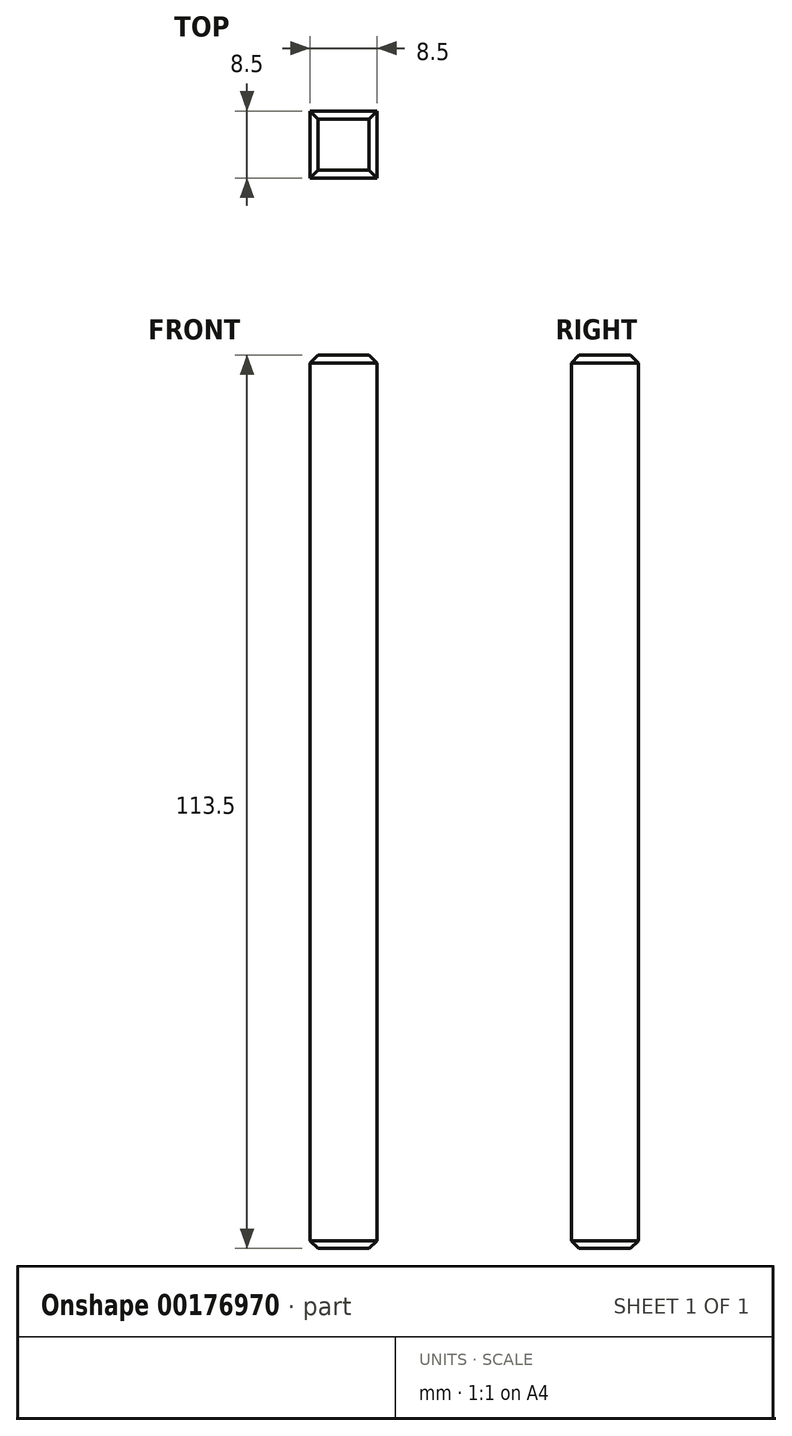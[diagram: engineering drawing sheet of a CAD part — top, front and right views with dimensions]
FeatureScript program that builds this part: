
annotation { "Feature Type Name" : "Feature", "Feature Type Description" : "" }
export const myFeature = defineFeature(function(context is Context, id is Id, definition is map)
    precondition{}
    {
        {
            var Q0;
            Q0=qCreatedBy(makeId("Top.planeOp"),FACE);
            var sketch = newSketch(context, id + "F0", { "sketchPlane" : qUnion([Q0])});
            skLineSegment(sketch, "E0.bottom", {"start": v(4.25, 4.25) * mm, "end": v(-4.25, 4.25) * mm});
            skLineSegment(sketch, "E0.top", {"start": v(4.25, -4.25) * mm, "end": v(-4.25, -4.25) * mm});
            skLineSegment(sketch, "E0.left", {"start": v(4.25, 4.25) * mm, "end": v(4.25, -4.25) * mm});
            skLineSegment(sketch, "E0.right", {"start": v(-4.25, 4.25) * mm, "end": v(-4.25, -4.25) * mm});
            skPoint(sketch, "E0.middle", {"position": v(0, 0) * mm});
            skSolve(sketch);
        }
        {
            var Q0;
            Q0 = qSketchRegion(id + "F0", true);
            extrude(context, id + "F1", {"entities" : qUnion([Q0]), "endBound" : BoundingType.SYMMETRIC, "depth" : 113.5 * mm});
        }
        {
            var Q0;
            Q0=makeQuery(id+"F1.opExtrude","CAP_EDGE",EDGE,{"disambiguationData":[OSD([sQuery(id+"F0.wireOp",EDGE,"E0.right")])],"isStart":false});
            var Q1;
            Q1=makeQuery(id+"F1.opExtrude","CAP_EDGE",EDGE,{"disambiguationData":[OSD([sQuery(id+"F0.wireOp",EDGE,"E0.top")])],"isStart":false});
            var Q2;
            Q2=makeQuery(id+"F1.opExtrude","CAP_EDGE",EDGE,{"disambiguationData":[OSD([sQuery(id+"F0.wireOp",EDGE,"E0.left")])],"isStart":false});
            var Q3;
            Q3=makeQuery(id+"F1.opExtrude","CAP_EDGE",EDGE,{"disambiguationData":[OSD([sQuery(id+"F0.wireOp",EDGE,"E0.bottom")])],"isStart":false});
            var Q4;
            Q4=makeQuery(id+"F1.opExtrude","CAP_EDGE",EDGE,{"disambiguationData":[OSD([sQuery(id+"F0.wireOp",EDGE,"E0.bottom")])],"isStart":true});
            var Q5;
            Q5=makeQuery(id+"F1.opExtrude","CAP_EDGE",EDGE,{"disambiguationData":[OSD([sQuery(id+"F0.wireOp",EDGE,"E0.right")])],"isStart":true});
            var Q6;
            Q6=makeQuery(id+"F1.opExtrude","CAP_EDGE",EDGE,{"disambiguationData":[OSD([sQuery(id+"F0.wireOp",EDGE,"E0.top")])],"isStart":true});
            var Q7;
            Q7=makeQuery(id+"F1.opExtrude","CAP_EDGE",EDGE,{"disambiguationData":[OSD([sQuery(id+"F0.wireOp",EDGE,"E0.left")])],"isStart":true});
            chamfer(context, id + "F2", {"entities" : qUnion([Q0, Q1, Q2, Q3, Q4, Q5, Q6, Q7]), "width" : 1 * mm, "tangentPropagation" : true});
        }
    });
